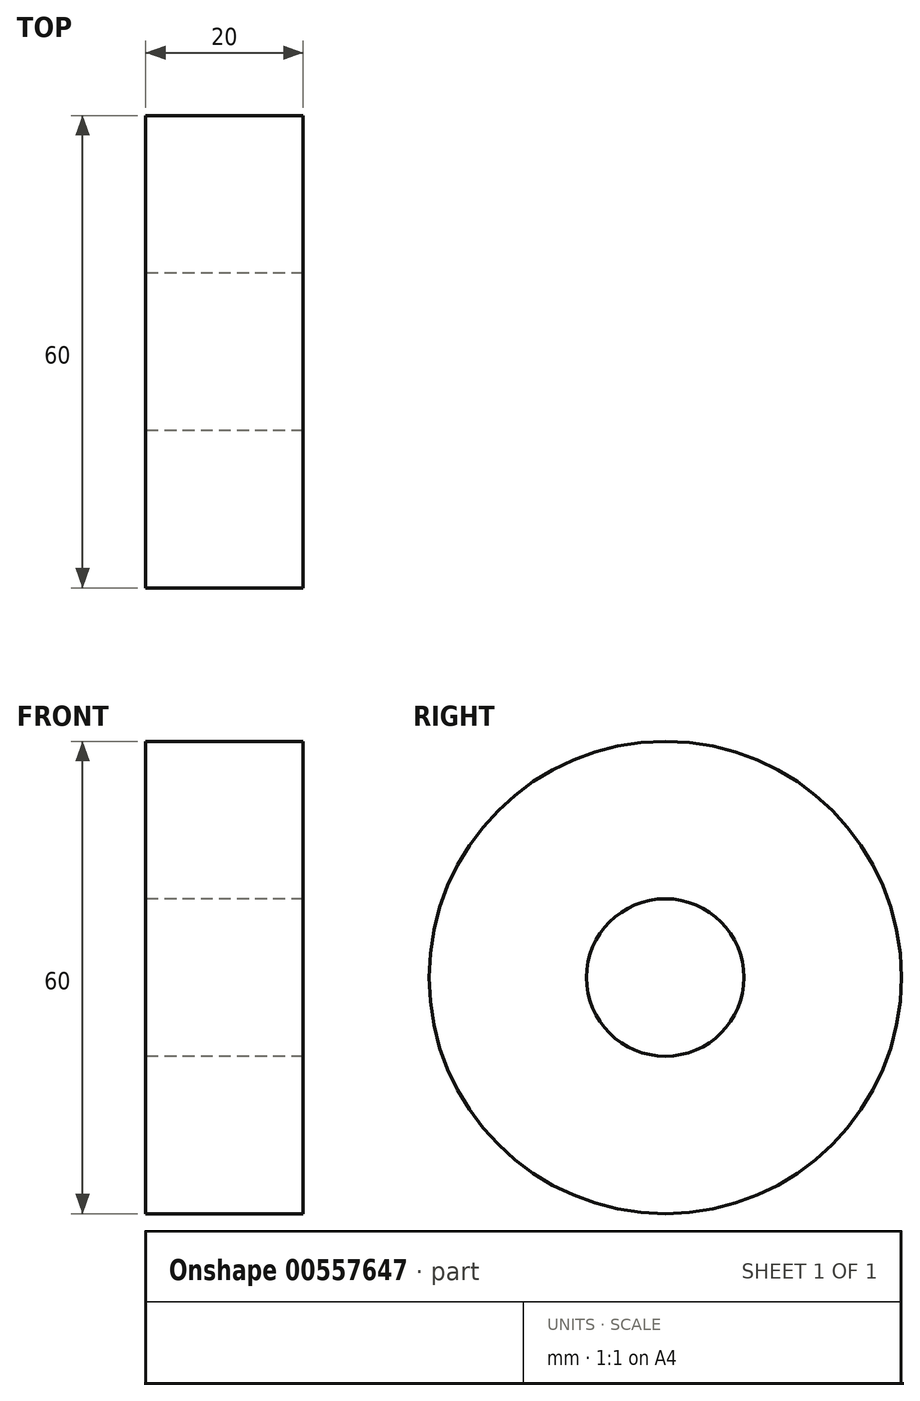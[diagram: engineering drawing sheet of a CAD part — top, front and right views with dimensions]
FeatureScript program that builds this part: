
annotation { "Feature Type Name" : "Feature", "Feature Type Description" : "" }
export const myFeature = defineFeature(function(context is Context, id is Id, definition is map)
    precondition{}
    {
        {
            var Q0;
            Q0=qCreatedBy(makeId("Right.planeOp"),FACE);
            var sketch = newSketch(context, id + "F0", { "sketchPlane" : qUnion([Q0])});
            skCircle(sketch, "E0", {"center": v(0, 0) * mm, "radius": 30 * mm});
            skCircle(sketch, "E1", {"center": v(0, 0) * mm, "radius": 10 * mm});
            skSolve(sketch);
        }
        {
            var Q0;
            Q0=makeQuery(id+"F0.imprint","IMPRINT",FACE,{"disambiguationData":[TD([[makeQuery(id+"F0.imprint","IMPRINT",EDGE,{"derivedFrom":sQuery(id+"F0.wireOp",EDGE,"E0")}),1.0]])]});
            extrude(context, id + "F1", {"entities" : qUnion([Q0]), "endBound" : BoundingType.SYMMETRIC, "depth" : 20 * mm, "offsetDistance" : 25 * mm});
        }
    });
